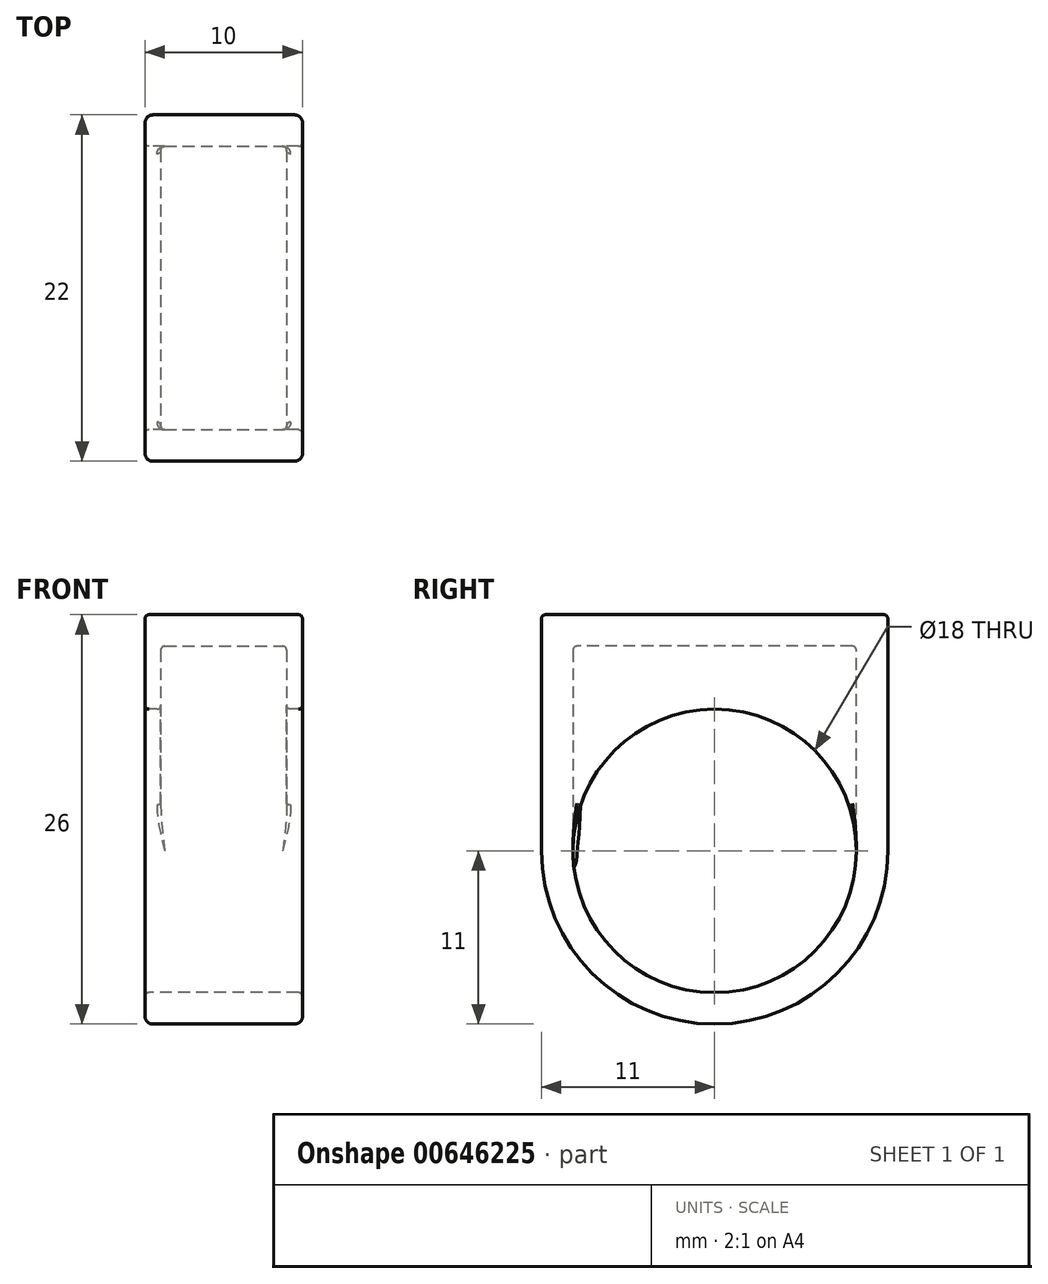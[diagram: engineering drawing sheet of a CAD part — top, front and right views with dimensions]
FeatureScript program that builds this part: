
annotation { "Feature Type Name" : "Feature", "Feature Type Description" : "" }
export const myFeature = defineFeature(function(context is Context, id is Id, definition is map)
    precondition{}
    {
        {
            var Q0;
            Q0=qCreatedBy(makeId("Right.planeOp"),FACE);
            var sketch = newSketch(context, id + "F0", { "sketchPlane" : qUnion([Q0])});
            skCircle(sketch, "E0", {"center": v(0, 0) * mm, "radius": 9 * mm});
            skArc(sketch, "E1", {"start": v(-11, 0) * mm, "mid": v(0, -11) * mm, "end": v(11, 0) * mm});
            skLineSegment(sketch, "E2", {"start": v(-9, 0) * mm, "end": v(-11, 0) * mm});
            skLineSegment(sketch, "E3", {"start": v(-11, 0) * mm, "end": v(-11, 15) * mm});
            skLineSegment(sketch, "E4", {"start": v(11, 0) * mm, "end": v(11, 15) * mm});
            skLineSegment(sketch, "E5", {"start": v(11, 15) * mm, "end": v(-11, 15) * mm});
            skSolve(sketch);
        }
        {
            var Q0;
            Q0=makeQuery(id+"F0.imprint","IMPRINT",FACE,{"disambiguationData":[TD([[makeQuery(id+"F0.imprint","IMPRINT",EDGE,{"derivedFrom":sQuery(id+"F0.wireOp",EDGE,"E0")}),-1.0]])]});
            extrude(context, id + "F1", {"entities" : qUnion([Q0]), "endBound" : BoundingType.SYMMETRIC, "depth" : 10 * mm, "offsetDistance" : 25 * mm});
        }
        {
            var Q0;
            Q0=qCreatedBy(makeId("Right.planeOp"),FACE);
            var sketch = newSketch(context, id + "F2", { "sketchPlane" : qUnion([Q0])});
            skLineSegment(sketch, "E6.0", {"start": v(-9, 13) * mm, "end": v(-9, 0) * mm});
            skLineSegment(sketch, "E6.1", {"start": v(9, 13) * mm, "end": v(-9, 13) * mm});
            skLineSegment(sketch, "E6.2", {"start": v(9, 0) * mm, "end": v(9, 13) * mm});
            skArc(sketch, "E6.3", {"start": v(-9, 0) * mm, "mid": v(0, -9) * mm, "end": v(9, 0) * mm});
            skLineSegment(sketch, "E7.0", {"start": v(9, 18) * mm, "end": v(-9, 18) * mm});
            skSolve(sketch);
        }
        {
            var Q0;
            Q0=makeQuery(id+"F2.imprint","IMPRINT",FACE,{"disambiguationData":[TD([[makeQuery(id+"F2.imprint","IMPRINT",EDGE,{"derivedFrom":sQuery(id+"F2.wireOp",EDGE,"E6.0")}),1.0]])]});
            extrude(context, id + "F3", {"entities" : qUnion([Q0]), "operationType" : NewBodyOperationType.REMOVE, "endBound" : BoundingType.SYMMETRIC, "oppositeDirection" : true, "depth" : 8 * mm, "offsetDistance" : 25 * mm});
        }
        {
            var Q0;
            Q0=makeQuery(id+"F1.opExtrude","CAP_EDGE",EDGE,{"disambiguationData":[OSD([sQuery(id+"F0.wireOp",EDGE,"E3")])],"isStart":true});
            var Q1;
            Q1=makeQuery(id+"F1.opExtrude","CAP_EDGE",EDGE,{"disambiguationData":[OSD([sQuery(id+"F0.wireOp",EDGE,"E3")])],"isStart":false});
            fillet(context, id + "F4", {"entities" : qUnion([Q0, Q1]), "radius" : 0.5 * mm, "tangentPropagation" : true, "allowEdgeOverflow" : false});
        }
        {
            var Q0;
            Q0=makeQuery(id+"F1.opExtrude","SWEPT_EDGE",EDGE,{"disambiguationData":[OSD([sQuery(id+"F0.wireOp",EDGE,"E4"),sQuery(id+"F0.wireOp",EDGE,"E5")])]});
            var Q1;
            Q1=makeQuery(id+"F1.opExtrude","SWEPT_EDGE",EDGE,{"disambiguationData":[OSD([sQuery(id+"F0.wireOp",EDGE,"E3"),sQuery(id+"F0.wireOp",EDGE,"E5")])]});
            var Q2;
            Q2=makeQuery(id+"F1.opExtrude","CAP_EDGE",EDGE,{"disambiguationData":[OSD([sQuery(id+"F0.wireOp",EDGE,"E0")])],"isStart":true});
            var Q3;
            Q3=makeQuery(id+"F1.opExtrude","CAP_EDGE",EDGE,{"disambiguationData":[OSD([sQuery(id+"F0.wireOp",EDGE,"E0")])],"isStart":false});
            var Q4;
            Q4=makeQuery(id+"F1.opExtrude","SWEPT_EDGE",EDGE,{"disambiguationData":[OSD([sQuery(id+"F0.wireOp",EDGE,"E1"),sQuery(id+"F0.wireOp",EDGE,"E3")])]});
            var Q5;
            Q5=makeQuery(id+"F3.boolean.opBoolean","COPY",EDGE,{"derivedFrom":makeQuery(id+"F3.opExtrude","SWEPT_EDGE",EDGE,{"disambiguationData":[OSD([sQuery(id+"F2.wireOp",EDGE,"E6.2"),sQuery(id+"F2.wireOp",EDGE,"E6.3")])]})});
            var Q6;
            Q6=makeQuery(id+"F3.boolean.opBoolean","INTERSECT",EDGE,{"derivedFrom":[makeQuery(id+"F1.opExtrude","SWEPT_FACE",FACE,{"disambiguationData":[OSD([sQuery(id+"F0.wireOp",EDGE,"E0")])]}),makeQuery(id+"F3.opExtrude","CAP_FACE",FACE,{"disambiguationData":[OSD([sQuery(id+"F2.wireOp",EDGE,"E6.0"),sQuery(id+"F2.wireOp",EDGE,"E6.1"),sQuery(id+"F2.wireOp",EDGE,"E6.2"),sQuery(id+"F2.wireOp",EDGE,"E6.3")])],"isStart":true})]});
            var Q7;
            {var subQ0=sQuery(id+"F0.wireOp",EDGE,"E1");Q7=makeQuery(id+"F4.opFillet","BLEND_EDGE",EDGE,{"blendedFrom":[makeQuery(id+"F1.opExtrude","CAP_EDGE",EDGE,{"disambiguationData":[OSD([subQ0])],"isStart":false}),makeQuery(id+"F1.opExtrude","CAP_FACE",FACE,{"disambiguationData":[OSD([sQuery(id+"F0.wireOp",EDGE,"E0"),subQ0,sQuery(id+"F0.wireOp",EDGE,"E3"),sQuery(id+"F0.wireOp",EDGE,"E4"),sQuery(id+"F0.wireOp",EDGE,"E5")])],"isStart":false})],"blendedInto":[makeQuery(id+"F1.opExtrude","CAP_FACE",FACE,{"disambiguationData":[OSD([sQuery(id+"F0.wireOp",EDGE,"E0"),subQ0,sQuery(id+"F0.wireOp",EDGE,"E3"),sQuery(id+"F0.wireOp",EDGE,"E4"),sQuery(id+"F0.wireOp",EDGE,"E5")])],"isStart":false})]});}
            var Q8;
            {var subQ0=sQuery(id+"F0.wireOp",EDGE,"E1");Q8=makeQuery(id+"F4.opFillet","BLEND_EDGE",EDGE,{"blendedFrom":[makeQuery(id+"F1.opExtrude","CAP_EDGE",EDGE,{"disambiguationData":[OSD([subQ0])],"isStart":false}),makeQuery(id+"F1.opExtrude","SWEPT_FACE",FACE,{"disambiguationData":[OSD([subQ0])]})],"blendedInto":[makeQuery(id+"F1.opExtrude","SWEPT_FACE",FACE,{"disambiguationData":[OSD([subQ0])]})]});}
            var Q9;
            Q9=makeQuery(id+"F1.opExtrude","CAP_EDGE",EDGE,{"disambiguationData":[OSD([sQuery(id+"F0.wireOp",EDGE,"E5")])],"isStart":true});
            var Q10;
            Q10=makeQuery(id+"F1.opExtrude","CAP_EDGE",EDGE,{"disambiguationData":[OSD([sQuery(id+"F0.wireOp",EDGE,"E5")])],"isStart":false});
            var Q11;
            Q11=makeQuery(id+"F4.opFillet","BLEND_EDGE",EDGE,{"blendedFrom":[makeQuery(id+"F1.opExtrude","CAP_EDGE",EDGE,{"disambiguationData":[OSD([sQuery(id+"F0.wireOp",EDGE,"E1")])],"isStart":true}),makeQuery(id+"F1.opExtrude","CAP_EDGE",EDGE,{"disambiguationData":[OSD([sQuery(id+"F0.wireOp",EDGE,"E3")])],"isStart":true})],"blendedInto":[]});
            var Q12;
            Q12=makeQuery(id+"F4.opFillet","BLEND_EDGE",EDGE,{"blendedFrom":[makeQuery(id+"F1.opExtrude","CAP_EDGE",EDGE,{"disambiguationData":[OSD([sQuery(id+"F0.wireOp",EDGE,"E1")])],"isStart":true}),makeQuery(id+"F1.opExtrude","CAP_EDGE",EDGE,{"disambiguationData":[OSD([sQuery(id+"F0.wireOp",EDGE,"E4")])],"isStart":true})],"blendedInto":[]});
            var Q13;
            {var subQ0=sQuery(id+"F0.wireOp",EDGE,"E1");Q13=makeQuery(id+"F4.opFillet","BLEND_EDGE",EDGE,{"blendedFrom":[makeQuery(id+"F1.opExtrude","CAP_EDGE",EDGE,{"disambiguationData":[OSD([subQ0])],"isStart":true}),makeQuery(id+"F1.opExtrude","CAP_FACE",FACE,{"disambiguationData":[OSD([sQuery(id+"F0.wireOp",EDGE,"E0"),subQ0,sQuery(id+"F0.wireOp",EDGE,"E3"),sQuery(id+"F0.wireOp",EDGE,"E4"),sQuery(id+"F0.wireOp",EDGE,"E5")])],"isStart":true})],"blendedInto":[makeQuery(id+"F1.opExtrude","CAP_FACE",FACE,{"disambiguationData":[OSD([sQuery(id+"F0.wireOp",EDGE,"E0"),subQ0,sQuery(id+"F0.wireOp",EDGE,"E3"),sQuery(id+"F0.wireOp",EDGE,"E4"),sQuery(id+"F0.wireOp",EDGE,"E5")])],"isStart":true})]});}
            var Q14;
            {var subQ0=sQuery(id+"F0.wireOp",EDGE,"E3");Q14=makeQuery(id+"F4.opFillet","BLEND_EDGE",EDGE,{"blendedFrom":[makeQuery(id+"F1.opExtrude","CAP_EDGE",EDGE,{"disambiguationData":[OSD([subQ0])],"isStart":true}),makeQuery(id+"F1.opExtrude","SWEPT_FACE",FACE,{"disambiguationData":[OSD([subQ0])]})],"blendedInto":[makeQuery(id+"F1.opExtrude","SWEPT_FACE",FACE,{"disambiguationData":[OSD([subQ0])]})]});}
            var Q15;
            Q15=makeQuery(id+"F1.opExtrude","SWEPT_EDGE",EDGE,{"disambiguationData":[OSD([sQuery(id+"F0.wireOp",EDGE,"E1"),sQuery(id+"F0.wireOp",EDGE,"E4")])]});
            var Q16;
            Q16=makeQuery(id+"F4.opFillet","BLEND_EDGE",EDGE,{"blendedFrom":[makeQuery(id+"F1.opExtrude","CAP_EDGE",EDGE,{"disambiguationData":[OSD([sQuery(id+"F0.wireOp",EDGE,"E3")])],"isStart":true}),makeQuery(id+"F1.opExtrude","SWEPT_FACE",FACE,{"disambiguationData":[OSD([sQuery(id+"F0.wireOp",EDGE,"E5")])]})],"blendedInto":[makeQuery(id+"F1.opExtrude","SWEPT_FACE",FACE,{"disambiguationData":[OSD([sQuery(id+"F0.wireOp",EDGE,"E5")])]})]});
            var Q17;
            {var subQ0=sQuery(id+"F0.wireOp",EDGE,"E3");Q17=makeQuery(id+"F4.opFillet","BLEND_EDGE",EDGE,{"blendedFrom":[makeQuery(id+"F1.opExtrude","CAP_EDGE",EDGE,{"disambiguationData":[OSD([subQ0])],"isStart":false}),makeQuery(id+"F1.opExtrude","CAP_FACE",FACE,{"disambiguationData":[OSD([sQuery(id+"F0.wireOp",EDGE,"E0"),sQuery(id+"F0.wireOp",EDGE,"E1"),subQ0,sQuery(id+"F0.wireOp",EDGE,"E4"),sQuery(id+"F0.wireOp",EDGE,"E5")])],"isStart":false})],"blendedInto":[makeQuery(id+"F1.opExtrude","CAP_FACE",FACE,{"disambiguationData":[OSD([sQuery(id+"F0.wireOp",EDGE,"E0"),sQuery(id+"F0.wireOp",EDGE,"E1"),subQ0,sQuery(id+"F0.wireOp",EDGE,"E4"),sQuery(id+"F0.wireOp",EDGE,"E5")])],"isStart":false})]});}
            var Q18;
            Q18=makeQuery(id+"F3.boolean.opBoolean","COPY",EDGE,{"derivedFrom":makeQuery(id+"F3.opExtrude","SWEPT_EDGE",EDGE,{"disambiguationData":[OSD([sQuery(id+"F2.wireOp",EDGE,"E6.1"),sQuery(id+"F2.wireOp",EDGE,"E6.2")])]})});
            var Q19;
            Q19=makeQuery(id+"F3.boolean.opBoolean","COPY",EDGE,{"derivedFrom":makeQuery(id+"F3.opExtrude","SWEPT_EDGE",EDGE,{"disambiguationData":[OSD([sQuery(id+"F2.wireOp",EDGE,"E6.0"),sQuery(id+"F2.wireOp",EDGE,"E6.3")])]})});
            var Q20;
            Q20=makeQuery(id+"F3.boolean.opBoolean","COPY",EDGE,{"derivedFrom":makeQuery(id+"F3.opExtrude","SWEPT_EDGE",EDGE,{"disambiguationData":[OSD([sQuery(id+"F2.wireOp",EDGE,"E6.0"),sQuery(id+"F2.wireOp",EDGE,"E6.1")])]})});
            var Q21;
            Q21=makeQuery(id+"F3.boolean.opBoolean","COPY",EDGE,{"derivedFrom":makeQuery(id+"F3.opExtrude","CAP_EDGE",EDGE,{"disambiguationData":[OSD([sQuery(id+"F2.wireOp",EDGE,"E6.1")])],"isStart":true})});
            var Q22;
            Q22=makeQuery(id+"F3.boolean.opBoolean","COPY",EDGE,{"derivedFrom":makeQuery(id+"F3.opExtrude","CAP_EDGE",EDGE,{"disambiguationData":[OSD([sQuery(id+"F2.wireOp",EDGE,"E6.1")])],"isStart":false})});
            var Q23;
            Q23=makeQuery(id+"F3.boolean.opBoolean","COPY",EDGE,{"derivedFrom":makeQuery(id+"F3.opExtrude","CAP_EDGE",EDGE,{"disambiguationData":[OSD([sQuery(id+"F2.wireOp",EDGE,"E6.2")])],"isStart":true})});
            var Q24;
            Q24=makeQuery(id+"F3.boolean.opBoolean","COPY",EDGE,{"derivedFrom":makeQuery(id+"F3.opExtrude","CAP_EDGE",EDGE,{"disambiguationData":[OSD([sQuery(id+"F2.wireOp",EDGE,"E6.2")])],"isStart":false})});
            var Q25;
            {var subQ0=sQuery(id+"F0.wireOp",EDGE,"E1");Q25=makeQuery(id+"F4.opFillet","BLEND_EDGE",EDGE,{"blendedFrom":[makeQuery(id+"F1.opExtrude","CAP_EDGE",EDGE,{"disambiguationData":[OSD([subQ0])],"isStart":true}),makeQuery(id+"F1.opExtrude","SWEPT_FACE",FACE,{"disambiguationData":[OSD([subQ0])]})],"blendedInto":[makeQuery(id+"F1.opExtrude","SWEPT_FACE",FACE,{"disambiguationData":[OSD([subQ0])]})]});}
            var Q26;
            Q26=makeQuery(id+"F4.opFillet","BLEND_EDGE",EDGE,{"blendedFrom":[makeQuery(id+"F1.opExtrude","CAP_EDGE",EDGE,{"disambiguationData":[OSD([sQuery(id+"F0.wireOp",EDGE,"E1")])],"isStart":false}),makeQuery(id+"F1.opExtrude","CAP_EDGE",EDGE,{"disambiguationData":[OSD([sQuery(id+"F0.wireOp",EDGE,"E3")])],"isStart":false})],"blendedInto":[]});
            var Q27;
            Q27=makeQuery(id+"F4.opFillet","BLEND_EDGE",EDGE,{"blendedFrom":[makeQuery(id+"F1.opExtrude","CAP_EDGE",EDGE,{"disambiguationData":[OSD([sQuery(id+"F0.wireOp",EDGE,"E1")])],"isStart":false}),makeQuery(id+"F1.opExtrude","CAP_EDGE",EDGE,{"disambiguationData":[OSD([sQuery(id+"F0.wireOp",EDGE,"E4")])],"isStart":false})],"blendedInto":[]});
            var Q28;
            {var subQ0=sQuery(id+"F0.wireOp",EDGE,"E3");Q28=makeQuery(id+"F4.opFillet","BLEND_EDGE",EDGE,{"blendedFrom":[makeQuery(id+"F1.opExtrude","CAP_EDGE",EDGE,{"disambiguationData":[OSD([subQ0])],"isStart":true}),makeQuery(id+"F1.opExtrude","CAP_FACE",FACE,{"disambiguationData":[OSD([sQuery(id+"F0.wireOp",EDGE,"E0"),sQuery(id+"F0.wireOp",EDGE,"E1"),subQ0,sQuery(id+"F0.wireOp",EDGE,"E4"),sQuery(id+"F0.wireOp",EDGE,"E5")])],"isStart":true})],"blendedInto":[makeQuery(id+"F1.opExtrude","CAP_FACE",FACE,{"disambiguationData":[OSD([sQuery(id+"F0.wireOp",EDGE,"E0"),sQuery(id+"F0.wireOp",EDGE,"E1"),subQ0,sQuery(id+"F0.wireOp",EDGE,"E4"),sQuery(id+"F0.wireOp",EDGE,"E5")])],"isStart":true})]});}
            var Q29;
            {var subQ0=sQuery(id+"F0.wireOp",EDGE,"E3");Q29=makeQuery(id+"F4.opFillet","BLEND_EDGE",EDGE,{"blendedFrom":[makeQuery(id+"F1.opExtrude","CAP_EDGE",EDGE,{"disambiguationData":[OSD([subQ0])],"isStart":false}),makeQuery(id+"F1.opExtrude","SWEPT_FACE",FACE,{"disambiguationData":[OSD([subQ0])]})],"blendedInto":[makeQuery(id+"F1.opExtrude","SWEPT_FACE",FACE,{"disambiguationData":[OSD([subQ0])]})]});}
            var Q30;
            Q30=makeQuery(id+"F4.opFillet","BLEND_EDGE",EDGE,{"blendedFrom":[makeQuery(id+"F1.opExtrude","CAP_EDGE",EDGE,{"disambiguationData":[OSD([sQuery(id+"F0.wireOp",EDGE,"E3")])],"isStart":false}),makeQuery(id+"F1.opExtrude","SWEPT_FACE",FACE,{"disambiguationData":[OSD([sQuery(id+"F0.wireOp",EDGE,"E5")])]})],"blendedInto":[makeQuery(id+"F1.opExtrude","SWEPT_FACE",FACE,{"disambiguationData":[OSD([sQuery(id+"F0.wireOp",EDGE,"E5")])]})]});
            var Q31;
            {var subQ0=sQuery(id+"F0.wireOp",EDGE,"E4");Q31=makeQuery(id+"F4.opFillet","BLEND_EDGE",EDGE,{"blendedFrom":[makeQuery(id+"F1.opExtrude","CAP_EDGE",EDGE,{"disambiguationData":[OSD([subQ0])],"isStart":true}),makeQuery(id+"F1.opExtrude","CAP_FACE",FACE,{"disambiguationData":[OSD([sQuery(id+"F0.wireOp",EDGE,"E0"),sQuery(id+"F0.wireOp",EDGE,"E1"),sQuery(id+"F0.wireOp",EDGE,"E3"),subQ0,sQuery(id+"F0.wireOp",EDGE,"E5")])],"isStart":true})],"blendedInto":[makeQuery(id+"F1.opExtrude","CAP_FACE",FACE,{"disambiguationData":[OSD([sQuery(id+"F0.wireOp",EDGE,"E0"),sQuery(id+"F0.wireOp",EDGE,"E1"),sQuery(id+"F0.wireOp",EDGE,"E3"),subQ0,sQuery(id+"F0.wireOp",EDGE,"E5")])],"isStart":true})]});}
            var Q32;
            {var subQ0=sQuery(id+"F0.wireOp",EDGE,"E4");Q32=makeQuery(id+"F4.opFillet","BLEND_EDGE",EDGE,{"blendedFrom":[makeQuery(id+"F1.opExtrude","CAP_EDGE",EDGE,{"disambiguationData":[OSD([subQ0])],"isStart":true}),makeQuery(id+"F1.opExtrude","SWEPT_FACE",FACE,{"disambiguationData":[OSD([subQ0])]})],"blendedInto":[makeQuery(id+"F1.opExtrude","SWEPT_FACE",FACE,{"disambiguationData":[OSD([subQ0])]})]});}
            var Q33;
            Q33=makeQuery(id+"F4.opFillet","BLEND_EDGE",EDGE,{"blendedFrom":[makeQuery(id+"F1.opExtrude","CAP_EDGE",EDGE,{"disambiguationData":[OSD([sQuery(id+"F0.wireOp",EDGE,"E4")])],"isStart":true}),makeQuery(id+"F1.opExtrude","SWEPT_FACE",FACE,{"disambiguationData":[OSD([sQuery(id+"F0.wireOp",EDGE,"E5")])]})],"blendedInto":[makeQuery(id+"F1.opExtrude","SWEPT_FACE",FACE,{"disambiguationData":[OSD([sQuery(id+"F0.wireOp",EDGE,"E5")])]})]});
            var Q34;
            {var subQ0=sQuery(id+"F0.wireOp",EDGE,"E4");Q34=makeQuery(id+"F4.opFillet","BLEND_EDGE",EDGE,{"blendedFrom":[makeQuery(id+"F1.opExtrude","CAP_EDGE",EDGE,{"disambiguationData":[OSD([subQ0])],"isStart":false}),makeQuery(id+"F1.opExtrude","CAP_FACE",FACE,{"disambiguationData":[OSD([sQuery(id+"F0.wireOp",EDGE,"E0"),sQuery(id+"F0.wireOp",EDGE,"E1"),sQuery(id+"F0.wireOp",EDGE,"E3"),subQ0,sQuery(id+"F0.wireOp",EDGE,"E5")])],"isStart":false})],"blendedInto":[makeQuery(id+"F1.opExtrude","CAP_FACE",FACE,{"disambiguationData":[OSD([sQuery(id+"F0.wireOp",EDGE,"E0"),sQuery(id+"F0.wireOp",EDGE,"E1"),sQuery(id+"F0.wireOp",EDGE,"E3"),subQ0,sQuery(id+"F0.wireOp",EDGE,"E5")])],"isStart":false})]});}
            var Q35;
            {var subQ0=sQuery(id+"F0.wireOp",EDGE,"E4");Q35=makeQuery(id+"F4.opFillet","BLEND_EDGE",EDGE,{"blendedFrom":[makeQuery(id+"F1.opExtrude","CAP_EDGE",EDGE,{"disambiguationData":[OSD([subQ0])],"isStart":false}),makeQuery(id+"F1.opExtrude","SWEPT_FACE",FACE,{"disambiguationData":[OSD([subQ0])]})],"blendedInto":[makeQuery(id+"F1.opExtrude","SWEPT_FACE",FACE,{"disambiguationData":[OSD([subQ0])]})]});}
            var Q36;
            Q36=makeQuery(id+"F4.opFillet","BLEND_EDGE",EDGE,{"blendedFrom":[makeQuery(id+"F1.opExtrude","CAP_EDGE",EDGE,{"disambiguationData":[OSD([sQuery(id+"F0.wireOp",EDGE,"E4")])],"isStart":false}),makeQuery(id+"F1.opExtrude","SWEPT_FACE",FACE,{"disambiguationData":[OSD([sQuery(id+"F0.wireOp",EDGE,"E5")])]})],"blendedInto":[makeQuery(id+"F1.opExtrude","SWEPT_FACE",FACE,{"disambiguationData":[OSD([sQuery(id+"F0.wireOp",EDGE,"E5")])]})]});
            var Q37;
            Q37=makeQuery(id+"F3.boolean.opBoolean","COPY",EDGE,{"derivedFrom":makeQuery(id+"F3.opExtrude","CAP_EDGE",EDGE,{"disambiguationData":[OSD([sQuery(id+"F2.wireOp",EDGE,"E6.0")])],"isStart":true})});
            var Q38;
            Q38=makeQuery(id+"F3.boolean.opBoolean","COPY",EDGE,{"derivedFrom":makeQuery(id+"F3.opExtrude","CAP_EDGE",EDGE,{"disambiguationData":[OSD([sQuery(id+"F2.wireOp",EDGE,"E6.0")])],"isStart":false})});
            var Q39;
            Q39=makeQuery(id+"F3.boolean.opBoolean","INTERSECT",EDGE,{"derivedFrom":[makeQuery(id+"F1.opExtrude","SWEPT_FACE",FACE,{"disambiguationData":[OSD([sQuery(id+"F0.wireOp",EDGE,"E0")])]}),makeQuery(id+"F3.opExtrude","CAP_FACE",FACE,{"disambiguationData":[OSD([sQuery(id+"F2.wireOp",EDGE,"E6.0"),sQuery(id+"F2.wireOp",EDGE,"E6.1"),sQuery(id+"F2.wireOp",EDGE,"E6.2"),sQuery(id+"F2.wireOp",EDGE,"E6.3")])],"isStart":false})]});
            fillet(context, id + "F5", {"entities" : qUnion([Q0, Q1, Q2, Q3, Q4, Q5, Q6, Q7, Q8, Q9, Q10, Q11, Q12, Q13, Q14, Q15, Q16, Q17, Q18, Q19, Q20, Q21, Q22, Q23, Q24, Q25, Q26, Q27, Q28, Q29, Q30, Q31, Q32, Q33, Q34, Q35, Q36, Q37, Q38, Q39]), "radius" : .25 * mm, "tangentPropagation" : true, "allowEdgeOverflow" : false});
        }
    });
